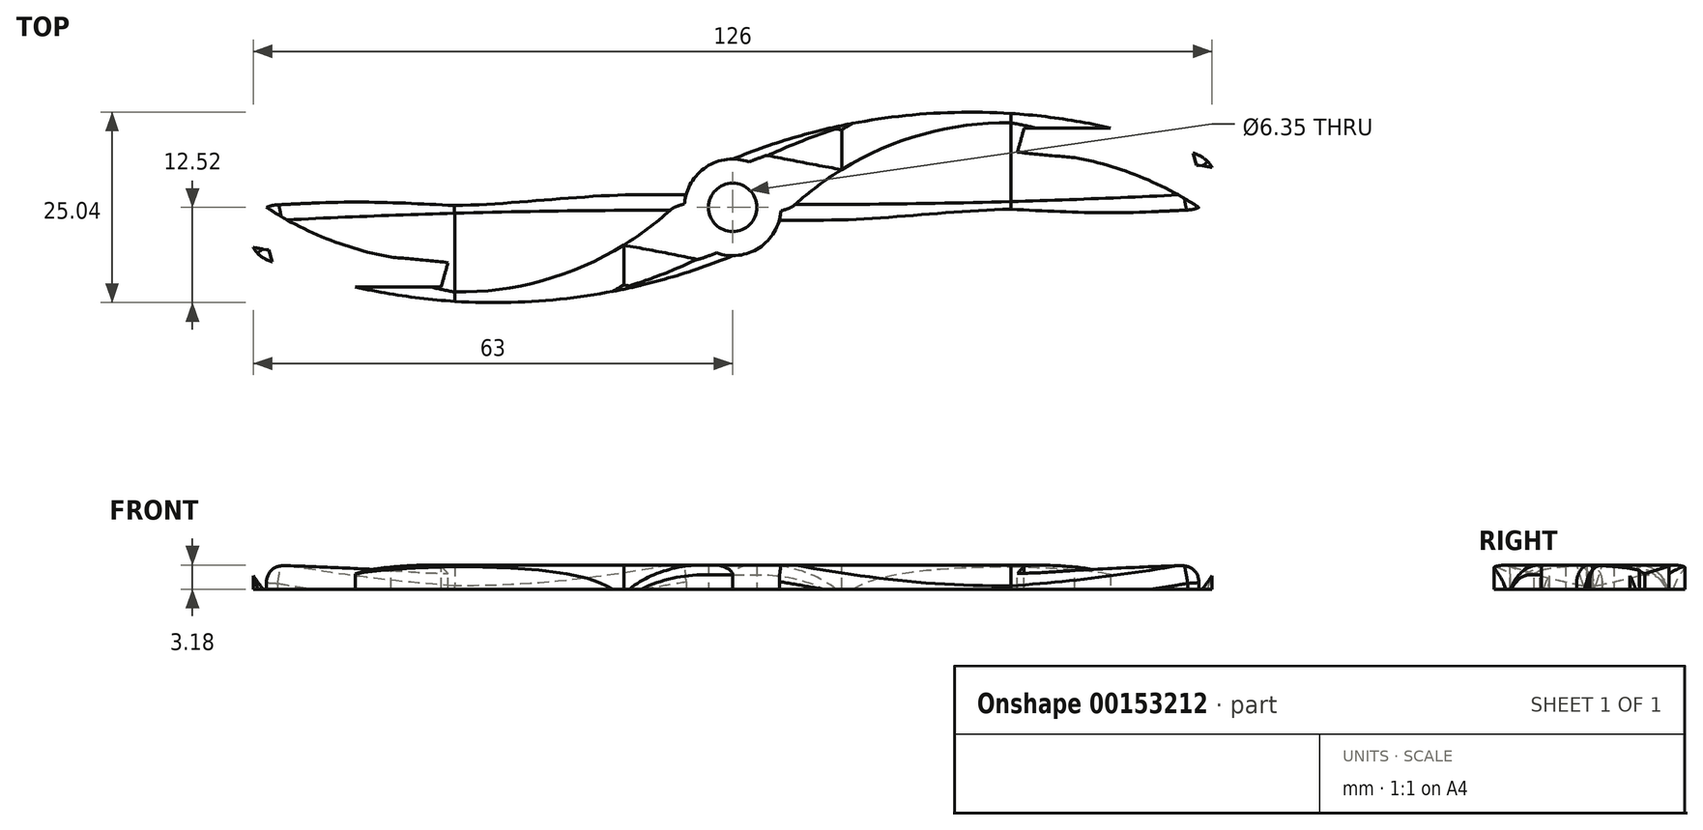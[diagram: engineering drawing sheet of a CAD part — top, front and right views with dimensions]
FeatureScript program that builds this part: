
annotation { "Feature Type Name" : "Feature", "Feature Type Description" : "" }
export const myFeature = defineFeature(function(context is Context, id is Id, definition is map)
    precondition{}
    {
        {
            var Q0;
            Q0=qCreatedBy(makeId("Top.planeOp"),FACE);
            var sketch = newSketch(context, id + "F0", { "sketchPlane" : qUnion([Q0])});
            skCircle(sketch, "E0", {"center": v(0, 0) * mm, "radius": 3.18 * mm});
            skCircle(sketch, "E1", {"center": v(0, 0) * mm, "radius": 6.35 * mm});
            skArc(sketch, "E2", {"start": v(59.8, -0.34) * mm, "mid": v(63.43, 2.8) * mm, "end": v(61.03, 6.96) * mm});
            skArc(sketch, "E3", {"start": v(61.03, 6.96) * mm, "mid": v(30.46, 12.51) * mm, "end": v(0, 6.35) * mm});
            skArc(sketch, "E4", {"start": v(6.12, -1.68) * mm, "mid": v(33.08, -1.37) * mm, "end": v(60, -0.33) * mm});
            skSolve(sketch);
        }
        {
            var Q0;
            Q0=qSketchRegion(id+"F0",true);
            extrude(context, id + "F1", {"entities" : qUnion([Q0]), "depth" : 3.17 * mm});
        }
        {
            var Q0;
            Q0=makeQuery(id+"F1.opExtrude","CAP_FACE",FACE,{"disambiguationData":[OSD([sQuery(id+"F0.wireOp",EDGE,"E0"),sQuery(id+"F0.wireOp",EDGE,"E1"),sQuery(id+"F0.wireOp",EDGE,"E2"),sQuery(id+"F0.wireOp",EDGE,"E3"),sQuery(id+"F0.wireOp",EDGE,"E4")])],"isStart":false});
            var sketch = newSketch(context, id + "F2", { "sketchPlane" : qUnion([Q0])});
            skArc(sketch, "E5", {"start": v(36.55, 11.12) * mm, "mid": v(20, 7.9) * mm, "end": v(6.12, -1.68) * mm});
            skArc(sketch, "E6", {"start": v(61.27, 0) * mm, "mid": v(49.6, 7.1) * mm, "end": v(36.55, 11.12) * mm});
            skArc(sketch, "E7.0", {"start": v(6.12, -1.68) * mm, "mid": v(32.97, -1.37) * mm, "end": v(59.8, -0.34) * mm});
            skArc(sketch, "E8.0", {"start": v(59.8, -0.34) * mm, "mid": v(60.56, -0.24) * mm, "end": v(61.27, 0) * mm});
            skPoint(sketch, "E9.orphan", {"position": v(61.03, 6.96) * mm});
            skSolve(sketch);
        }
        {
            var Q0;
            Q0=qCreatedBy(makeId("Right.planeOp"),FACE);
            var sketch = newSketch(context, id + "F3", { "sketchPlane" : qUnion([Q0])});
            skPoint(sketch, "E10.0", {"position": v(11.12, 3.18) * mm});
            skLineSegment(sketch, "E11", {"start": v(12.52, 3.18) * mm, "end": v(12.52, 0) * mm});
            skLineSegment(sketch, "E12.0.0", {"start": v(-0.34, 0) * mm, "end": v(6.96, 0) * mm});
            skLineSegment(sketch, "E12.0.1", {"start": v(6.96, 0) * mm, "end": v(6.96, 3.18) * mm});
            skLineSegment(sketch, "E12.0.2", {"start": v(6.96, 3.18) * mm, "end": v(-0.34, 3.18) * mm});
            skLineSegment(sketch, "E12.0.3", {"start": v(-0.34, 3.18) * mm, "end": v(-0.34, 0) * mm});
            skLineSegment(sketch, "E13", {"start": v(-6.35, 0) * mm, "end": v(-6.35, 3.18) * mm});
            skLineSegment(sketch, "E14.0", {"start": v(-1.68, 3.18) * mm, "end": v(-1.68, 0) * mm});
            skLineSegment(sketch, "E15.0", {"start": v(11.13, 3.18) * mm, "end": v(-1.68, 3.18) * mm});
            skLineSegment(sketch, "E16", {"start": v(-1.68, 0) * mm, "end": v(-1.68, 3.18) * mm});
            skArc(sketch, "E17", {"start": v(-1.68, 0) * mm, "mid": v(4.78, 1.34) * mm, "end": v(11.13, 3.17) * mm});
            skSolve(sketch);
        }
        {
            var Q0;
            Q0=makeQuery(id+"F2.imprint","IMPRINT",FACE,{"disambiguationData":[TD([[makeQuery(id+"F2.imprint","IMPRINT",EDGE,{"derivedFrom":sQuery(id+"F2.wireOp",EDGE,"E5")}),1.0]])]});
            var Q1;
            Q1=sQuery(id+"F3.wireOp",EDGE,"E17");
            sweep(context, id + "F4", {"operationType" : NewBodyOperationType.REMOVE, "profiles" : qUnion([Q0]), "path" : qUnion([Q1])});
        }
        {
            var Q0;
            Q0=makeQuery(id+"F1.opExtrude","CAP_FACE",FACE,{"disambiguationData":[OSD([sQuery(id+"F0.wireOp",EDGE,"E0"),sQuery(id+"F0.wireOp",EDGE,"E1"),sQuery(id+"F0.wireOp",EDGE,"E2"),sQuery(id+"F0.wireOp",EDGE,"E3"),sQuery(id+"F0.wireOp",EDGE,"E4")])],"isStart":false});
            var sketch = newSketch(context, id + "F5", { "sketchPlane" : qUnion([Q0])});
            skArc(sketch, "E18.0", {"start": v(61.03, 6.96) * mm, "mid": v(30.46, 12.51) * mm, "end": v(0, 6.35) * mm});
            skPoint(sketch, "E19.endSnap0", {"position": v(63.48, 3.56) * mm});
            skArc(sketch, "E20.0", {"start": v(61.27, 0) * mm, "mid": v(63.48, 3.56) * mm, "end": v(61.03, 6.96) * mm});
            skArc(sketch, "E21", {"start": v(2.4, 7.3) * mm, "mid": v(31.68, 2.36) * mm, "end": v(61.27, 0) * mm});
            skSolve(sketch);
        }
        {
            var Q0;
            Q0=qCreatedBy(makeId("Right.planeOp"),FACE);
            var sketch = newSketch(context, id + "F6", { "sketchPlane" : qUnion([Q0])});
            skLineSegment(sketch, "E22", {"start": v(-6.35, 0) * mm, "end": v(-6.35, 3.18) * mm});
            skLineSegment(sketch, "E23.0.0", {"start": v(6.96, 3.18) * mm, "end": v(0, 3.18) * mm});
            skFitSpline(sketch, "E23.0.1", {"points": [v(0, 3.18) * mm, v(-0.21, 3.06) * mm, v(-0.32, 2.96) * mm, v(-0.34, 2.88) * mm]});
            skLineSegment(sketch, "E23.0.2", {"start": v(-0.34, 2.88) * mm, "end": v(-0.34, 0) * mm});
            skLineSegment(sketch, "E23.0.3", {"start": v(-0.34, 0) * mm, "end": v(6.96, 0) * mm});
            skLineSegment(sketch, "E23.0.4", {"start": v(6.96, 0) * mm, "end": v(6.96, 3.18) * mm});
            skLineSegment(sketch, "E24", {"start": v(12.52, 3.18) * mm, "end": v(12.52, 0) * mm});
            skLineSegment(sketch, "E25", {"start": v(-1.68, 0) * mm, "end": v(-1.68, 2.8) * mm});
            skLineSegment(sketch, "E26.0", {"start": v(-1.68, 3.18) * mm, "end": v(11.13, 3.18) * mm});
            skFitSpline(sketch, "E27", {"points": [v(11.13, 3.18) * mm, v(7.08, 1.84) * mm, v(2.91, 0.8) * mm, v(-1.3, 0.07) * mm]});
            skArc(sketch, "E28.0", {"start": v(11.12, 3.17) * mm, "mid": v(4.98, 1.4) * mm, "end": v(-1.28, 0.07) * mm});
            skArc(sketch, "E29", {"start": v(12.52, 0) * mm, "mid": v(10.16, 2.33) * mm, "end": v(6.96, 3.17) * mm});
            skSolve(sketch);
        }
        {
            var Q0;
            {var subQ7=sQuery(id+"F5.wireOp",EDGE,"E20.0");Q0=makeQuery(id+"F5.imprint","IMPRINT",FACE,{"disambiguationData":[TD([[makeQuery(id+"F5.imprint","IMPRINT",EDGE,{"derivedFrom":subQ7}),1.0]])]});}
            var Q1;
            {var subQ1=sQuery(id+"F3.wireOp",VERTEX,"E17.end");var subQ2=makeQuery(id+"F4.boolean.opBoolean","COPY",EDGE,{"derivedFrom":makeQuery(id+"F4.opSweep","CAP_EDGE",EDGE,{"disambiguationData":[OSD([sQuery(id+"F2.wireOp",EDGE,"E6"),subQ1])],"isStart":true})});Q1=makeQuery(id+"F5.imprint","IMPRINT",FACE,{"disambiguationData":[TD([[makeQuery(id+"F5.imprint","IMPRINT",EDGE,{"derivedFrom":subQ2}),-1.0]])]});}
            var Q2;
            Q2=sQuery(id+"F6.wireOp",EDGE,"E29");
            sweep(context, id + "F7", {"operationType" : NewBodyOperationType.REMOVE, "profiles" : qUnion([Q0, Q1]), "path" : qUnion([Q2]), "keepProfileOrientation" : true});
        }
        {
            var Q0;
            Q0=qCreatedBy(makeId("Top.planeOp"),FACE);
            var sketch = newSketch(context, id + "F8", { "sketchPlane" : qUnion([Q0])});
            skFitSpline(sketch, "E30.0.2", {"points": [v(36.55, 5.96) * mm, v(37.6, 5.82) * mm, v(39.72, 5.52) * mm, v(42.88, 5.04) * mm, v(46.04, 4.5) * mm, v(49.18, 3.92) * mm, v(51.79, 3.36) * mm, v(53.85, 2.86) * mm, v(55.4, 2.44) * mm, v(56.92, 1.99) * mm, v(58.44, 1.47) * mm, v(59.67, 0.95) * mm, v(60.61, 0.46) * mm, v(61.06, 0.17) * mm, v(61.27, 0) * mm]});
            skFitSpline(sketch, "E30.0.3", {"points": [v(61.27, 0) * mm, v(1000, 61.27) * mm, v(2.26, 1000) * mm, v(61.27, 4.4) * mm]});
            skArc(sketch, "E31.0.0", {"start": v(61.27, 0) * mm, "mid": v(60.56, -0.24) * mm, "end": v(59.8, -0.34) * mm});
            skFitSpline(sketch, "E31.0.1", {"points": [v(61.27, 0) * mm, v(61.06, 0.17) * mm, v(60.61, 0.46) * mm, v(59.67, 0.95) * mm, v(58.44, 1.47) * mm, v(56.92, 1.99) * mm, v(55.4, 2.44) * mm, v(53.85, 2.86) * mm, v(51.79, 3.36) * mm, v(49.18, 3.92) * mm, v(46.04, 4.5) * mm, v(42.88, 5.04) * mm, v(39.72, 5.52) * mm, v(37.6, 5.82) * mm, v(36.55, 5.96) * mm]});
            skArc(sketch, "E31.0.3", {"start": v(59.8, -0.34) * mm, "mid": v(48.18, -0.87) * mm, "end": v(36.55, -1.28) * mm});
            skArc(sketch, "E32.0.0", {"start": v(62.26, 6.2) * mm, "mid": v(61.8, 5.84) * mm, "end": v(61.27, 5.56) * mm});
            skFitSpline(sketch, "E32.0.1", {"points": [v(61.27, 5.56) * mm, v(1000, 61.27) * mm, v(4.4, 1000) * mm, v(61.27, 2.26) * mm]});
            skArc(sketch, "E32.0.2", {"start": v(61.27, 0) * mm, "mid": v(62.65, 1.08) * mm, "end": v(63.4, 2.66) * mm});
            skArc(sketch, "E33", {"start": v(61.27, 0) * mm, "mid": v(49.87, 5.34) * mm, "end": v(37.42, 7.26) * mm});
            skFitSpline(sketch, "E34.0.2", {"points": [v(36.55, 5.96) * mm, v(37.6, 5.82) * mm, v(39.72, 5.52) * mm, v(42.88, 5.04) * mm, v(46.04, 4.5) * mm, v(49.18, 3.92) * mm, v(51.79, 3.36) * mm, v(53.85, 2.86) * mm, v(55.4, 2.44) * mm, v(56.92, 1.99) * mm, v(58.44, 1.47) * mm, v(59.67, 0.95) * mm, v(60.61, 0.46) * mm, v(61.06, 0.17) * mm, v(61.27, 0) * mm]});
            skArc(sketch, "E34.0.4", {"start": v(61.27, 5.56) * mm, "mid": v(49.33, 6.2) * mm, "end": v(37.42, 7.26) * mm});
            skArc(sketch, "E35.0", {"start": v(44.93, 6.54) * mm, "mid": v(41.17, 6.88) * mm, "end": v(37.42, 7.26) * mm});
            skFitSpline(sketch, "E36.0.1", {"points": [v(61.27, 5.56) * mm, v(1000, 61.27) * mm, v(4.4, 1000) * mm, v(61.27, 2.26) * mm]});
            skArc(sketch, "E36.0.3", {"start": v(62.26, 6.2) * mm, "mid": v(63.3, 4.59) * mm, "end": v(63.4, 2.66) * mm});
            skLineSegment(sketch, "E37", {"start": v(37.42, 7.26) * mm, "end": v(38.31, 10.45) * mm});
            skLineSegment(sketch, "E38", {"start": v(38.31, 10.45) * mm, "end": v(70.21, 10.45) * mm});
            skLineSegment(sketch, "E39", {"start": v(70.21, 10.45) * mm, "end": v(70.21, 0) * mm});
            skLineSegment(sketch, "E40", {"start": v(70.21, 0) * mm, "end": v(61.27, 0) * mm});
            skPoint(sketch, "E34.0.5.end.orphan", {"position": v(13.74, 10.63) * mm});
            skPoint(sketch, "E34.0.0.end.orphan", {"position": v(2.4, 7.3) * mm});
            skPoint(sketch, "E30.0.1.start.orphan", {"position": v(14.32, 4.97) * mm});
            skSolve(sketch);
        }
        {
            var Q0;
            Q0=qSketchRegion(id+"F8",true);
            extrude(context, id + "F9", {"entities" : qUnion([Q0]), "operationType" : NewBodyOperationType.REMOVE, "oppositeDirection" : true, "depth" : 25.4 * mm, "hasSecondDirection" : true, "secondDirectionOppositeDirection" : false, "secondDirectionDepth" : 25.4 * mm});
        }
        {
            var Q0;
            Q0=makeQuery(id+"F4.boolean.opBoolean","INTERSECT",EDGE,{"derivedFrom":[makeQuery(id+"F1.opExtrude","SWEPT_FACE",FACE,{"disambiguationData":[OSD([sQuery(id+"F0.wireOp",EDGE,"E2")])]}),makeQuery(id+"F4.opSweep","SWEPT_FACE",FACE,{"disambiguationData":[OSD([sQuery(id+"F2.wireOp",EDGE,"E6"),sQuery(id+"F3.wireOp",EDGE,"E17")])]})]});
            var Q1;
            Q1=makeQuery(id+"F4.boolean.opBoolean","INTERSECT",EDGE,{"derivedFrom":[makeQuery(id+"F1.opExtrude","SWEPT_FACE",FACE,{"disambiguationData":[OSD([sQuery(id+"F0.wireOp",EDGE,"E4")])]}),makeQuery(id+"F4.opSweep","SWEPT_FACE",FACE,{"disambiguationData":[OSD([sQuery(id+"F2.wireOp",EDGE,"E6"),sQuery(id+"F3.wireOp",EDGE,"E17")])]})]});
            var Q2;
            Q2=makeQuery(id+"F4.boolean.opBoolean","INTERSECT",EDGE,{"derivedFrom":[makeQuery(id+"F1.opExtrude","SWEPT_FACE",FACE,{"disambiguationData":[OSD([sQuery(id+"F0.wireOp",EDGE,"E4")])]}),makeQuery(id+"F4.opSweep","SWEPT_FACE",FACE,{"disambiguationData":[OSD([sQuery(id+"F2.wireOp",EDGE,"E5"),sQuery(id+"F3.wireOp",EDGE,"E17")])]})]});
            fillet(context, id + "F10", {"entities" : qUnion([Q0, Q1, Q2]), "radius" : 2.54 * mm, "tangentPropagation" : true, "allowEdgeOverflow" : false});
        }
        {
            var Q0;
            Q0=makeQuery(id+"F9.boolean.opBoolean","INTERSECT",EDGE,{"derivedFrom":[makeQuery(id+"F7.boolean.opBoolean","COPY",FACE,{"derivedFrom":makeQuery(id+"F7.opSweep","SWEPT_FACE",FACE,{"disambiguationData":[OSD([sQuery(id+"F5.wireOp",EDGE,"E21"),sQuery(id+"F6.wireOp",EDGE,"E29")])]})}),makeQuery(id+"F9.opExtrude","SWEPT_FACE",FACE,{"disambiguationData":[OSD([sQuery(id+"F8.wireOp",EDGE,"E33")])]})]});
            var Q1;
            Q1=makeQuery(id+"F7.boolean.opBoolean","COPY",EDGE,{"derivedFrom":makeQuery(id+"F7.opSweep","CAP_EDGE",EDGE,{"disambiguationData":[OSD([sQuery(id+"F5.wireOp",EDGE,"E21"),sQuery(id+"F6.wireOp",VERTEX,"E29.start")])],"isStart":false})});
            var Q2;
            Q2=makeQuery(id+"F7.boolean.opBoolean","INTERSECT",EDGE,{"derivedFrom":[makeQuery(id+"F1.opExtrude","SWEPT_FACE",FACE,{"disambiguationData":[OSD([sQuery(id+"F0.wireOp",EDGE,"E3")])]}),makeQuery(id+"F7.opSweep","SWEPT_FACE",FACE,{"disambiguationData":[OSD([sQuery(id+"F5.wireOp",EDGE,"E21"),sQuery(id+"F6.wireOp",EDGE,"E29")])]})]});
            fillet(context, id + "F11", {"entities" : qUnion([Q0, Q1, Q2]), "radius" : 1.27 * mm, "tangentPropagation" : true, "allowEdgeOverflow" : false});
        }
        {
            var Q0;
            Q0=qCreatedBy(makeId("Right.planeOp"),FACE);
            var sketch = newSketch(context, id + "F12", { "sketchPlane" : qUnion([Q0])});
            skLineSegment(sketch, "E41", {"start": v(0, 0) * mm, "end": v(0, 36.39) * mm});
            skSolve(sketch);
        }
        {
            var Q0;
            Q0=makeQuery(id+"F1.opExtrude","SWEPT_BODY",BODY,{"disambiguationData":[OSD([sQuery(id+"F0.wireOp",EDGE,"E0"),sQuery(id+"F0.wireOp",EDGE,"E1"),sQuery(id+"F0.wireOp",EDGE,"E2"),sQuery(id+"F0.wireOp",EDGE,"E3"),sQuery(id+"F0.wireOp",EDGE,"E4")])]});
            var Q1;
            Q1=sQuery(id+"F12.wireOp",EDGE,"E41");
            circularPattern(context, id + "F13", {"operationType" : NewBodyOperationType.ADD, "entities" : qUnion([Q0]), "axis" : qUnion([Q1]), "angle" : 360 * degree, "instanceCount" : 2, "equalSpace" : true});
        }
    });
